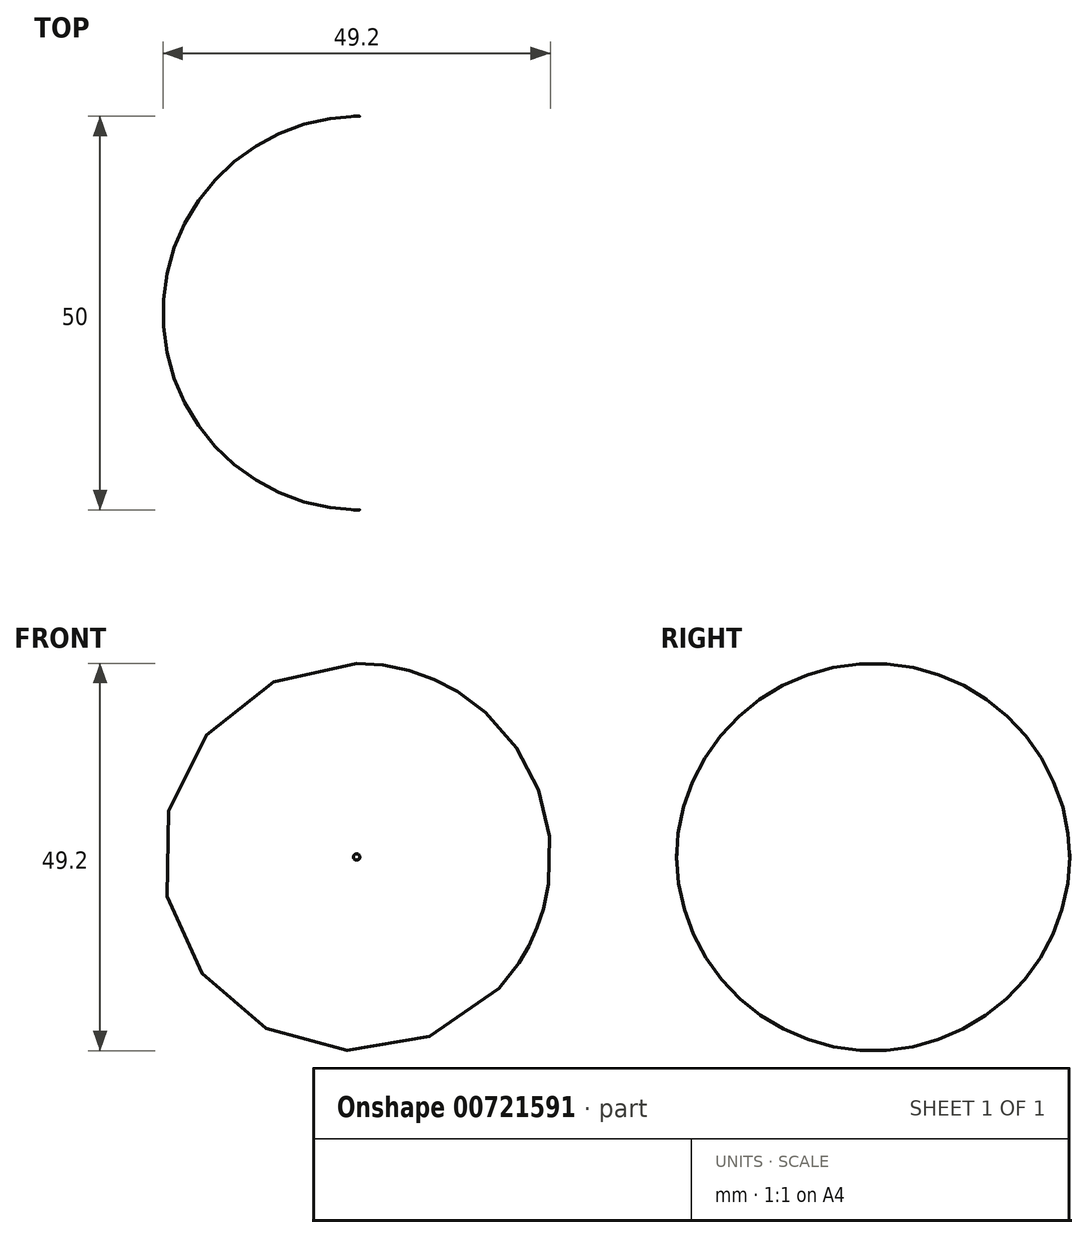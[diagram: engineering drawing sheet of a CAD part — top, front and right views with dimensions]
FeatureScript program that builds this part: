
annotation { "Feature Type Name" : "Feature", "Feature Type Description" : "" }
export const myFeature = defineFeature(function(context is Context, id is Id, definition is map)
    precondition{}
    {
        {
            var Q0;
            Q0=qCreatedBy(makeId("Front.planeOp"),FACE);
            var sketch = newSketch(context, id + "F0", { "sketchPlane" : qUnion([Q0])});
            skCircle(sketch, "E0", {"center": v(0, 0) * mm, "radius": 25.4 * mm});
            skSolve(sketch);
        }
        {
            var Q0;
            Q0=makeQuery(id+"F0.imprint","IMPRINT",FACE,{"disambiguationData":[TD([[makeQuery(id+"F0.imprint","IMPRINT",EDGE,{"derivedFrom":sQuery(id+"F0.wireOp",EDGE,"E0")}),1.0]])]});
            extrude(context, id + "F1", {"entities" : qUnion([Q0]), "oppositeDirection" : true, "depth" : 25 * mm, "offsetDistance" : 25.4 * mm});
        }
        {
            var Q0;
            Q0=makeQuery(id+"F1.opExtrude","CAP_FACE",FACE,{"disambiguationData":[OSD([sQuery(id+"F0.wireOp",EDGE,"E0")])],"isStart":true});
            fillet(context, id + "F2", {"entities" : qUnion([Q0]), "radius" : 25 * mm, "tangentPropagation" : true, "allowEdgeOverflow" : false});
        }
        {
            var Q0;
            Q0=makeQuery(id+"F1.opExtrude","CAP_FACE",FACE,{"disambiguationData":[OSD([sQuery(id+"F0.wireOp",EDGE,"E0")])],"isStart":false});
            extrude(context, id + "F3", {"entities" : qUnion([Q0]), "operationType" : NewBodyOperationType.ADD, "depth" : 25 * mm, "offsetDistance" : 25 * mm});
        }
        {
            var Q0;
            Q0=makeQuery(id+"F3.opExtrude","CAP_FACE",FACE,{"disambiguationData":[OSD([sQuery(id+"F0.wireOp",EDGE,"E0")])],"isStart":false});
            fillet(context, id + "F4", {"entities" : qUnion([Q0]), "radius" : 25 * mm, "tangentPropagation" : true, "allowEdgeOverflow" : false});
        }
    });
